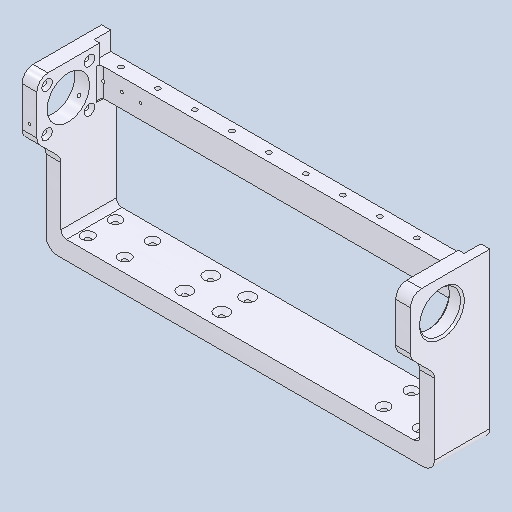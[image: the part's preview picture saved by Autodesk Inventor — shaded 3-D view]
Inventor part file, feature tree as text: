
AUTODESK INVENTOR PART (.ipt)
format: ipt  version: 2024.1 (Build 281209000, 209)  size: 388,608 bytes
history: native  units: mm
features: sketch x4, other x3, extrude x1
ambient origin geometry x8: Origin, YZ Plane, XZ Plane, XY Plane, X Axis, Y Axis, Z Axis, Center Point
bodies: Solid1 (feature_tree)
feature tree (8):
  other  "gantry_L.ipt"
  extrude  "Extrusion1"  Depth=10.0mm
  other  "Solid1::gantry_L.ipt"
  other  "TaggingFeature1"
  sketch  "Sketch1"  dims[d0=10.0mm d1=1.6mm]
  sketch  "Sketch2"  dims[d2=1.6mm]
  sketch  "Sketch3"  dims[d3=1.6mm]
  sketch  "Sketch16"  dims[d4=1.6mm d5=4.0mm d6=13.0mm d7=7.0mm d8=10.0mm d9=7.0mm d10=7.0mm d11=10.0mm d12=10.0mm d13=0.0mm d14=0.0mm]
